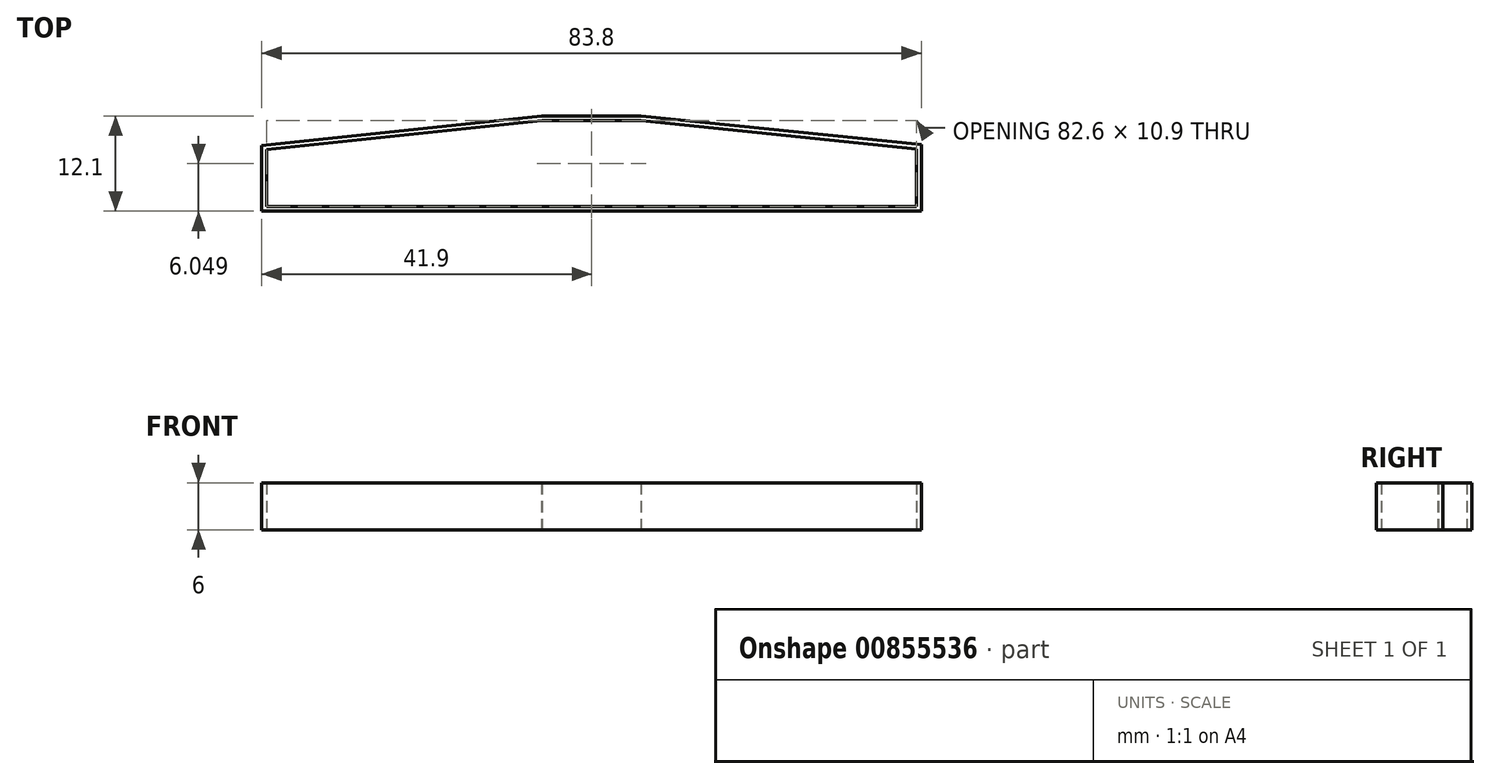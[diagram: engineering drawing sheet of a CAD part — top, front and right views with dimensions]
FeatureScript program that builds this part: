
annotation { "Feature Type Name" : "Feature", "Feature Type Description" : "" }
export const myFeature = defineFeature(function(context is Context, id is Id, definition is map)
    precondition{}
    {
        {
            var Q0;
            Q0=qCreatedBy(makeId("Top.planeOp"),FACE);
            var sketch = newSketch(context, id + "F0", { "sketchPlane" : qUnion([Q0])});
            skLineSegment(sketch, "E0", {"start": v(0, 1.99) * mm, "end": v(-41.5, 1.99) * mm});
            skLineSegment(sketch, "E1", {"start": v(-41.5, 1.99) * mm, "end": v(-41.5, 9.19) * mm});
            skLineSegment(sketch, "E2", {"start": v(-41.5, 9.19) * mm, "end": v(-6.5, 12.89) * mm});
            skLineSegment(sketch, "E3", {"start": v(-6.5, 12.89) * mm, "end": v(6.08, 12.89) * mm});
            skLineSegment(sketch, "E4", {"start": v(6.08, 12.89) * mm, "end": v(41.1, 9.29) * mm});
            skLineSegment(sketch, "E5", {"start": v(41.1, 9.29) * mm, "end": v(41.1, 1.99) * mm});
            skLineSegment(sketch, "E6", {"start": v(41.1, 1.99) * mm, "end": v(0, 1.99) * mm});
            skLineSegment(sketch, "E7.0", {"start": v(-42.1, 1.39) * mm, "end": v(-42.1, 9.73) * mm});
            skLineSegment(sketch, "E7.1", {"start": v(-0.5, 1.39) * mm, "end": v(-42.1, 1.39) * mm});
            skLineSegment(sketch, "E7.2", {"start": v(-6.53, 13.49) * mm, "end": v(6.12, 13.49) * mm});
            skLineSegment(sketch, "E7.3", {"start": v(6.12, 13.49) * mm, "end": v(41.7, 9.83) * mm});
            skLineSegment(sketch, "E7.4", {"start": v(41.7, 9.83) * mm, "end": v(41.7, 1.39) * mm});
            skLineSegment(sketch, "E7.5", {"start": v(-42.1, 9.73) * mm, "end": v(-6.53, 13.49) * mm});
            skLineSegment(sketch, "E7.6", {"start": v(41.7, 1.39) * mm, "end": v(-0.5, 1.39) * mm});
            skSolve(sketch);
        }
        {
            var Q0;
            Q0=makeQuery(id+"F0.imprint","IMPRINT",FACE,{"disambiguationData":[TD([[makeQuery(id+"F0.imprint","IMPRINT",EDGE,{"derivedFrom":sQuery(id+"F0.wireOp",EDGE,"E0")}),1.0]])]});
            var Q1;
            Q1 = qConstructionFilter(qBodyType(qCreatedBy(id + "F0" ,EDGE), BodyType.WIRE), ConstructionObject.NO);
            extrude(context, id + "F1", {"entities" : qUnion([Q0]), "surfaceEntities" : qUnion([Q1]), "depth" : 6 * mm, "offsetDistance" : 25 * mm});
        }
    });
